# Revit family: Screen-Desk_Mounted-Teknion-JNSASW-Solid_Add-On-R2015
name_source: partatom
category: Furniture
revit_build: Autodesk Revit 2018 (Build: 20190510_1515(x64)
units: mm (PartAtom-declared; Revit-internal decimal feet)

## family parameters
Always vertical = Yes
Cut with Voids When Loaded = No
OmniClass Number = 23.40.20.00
OmniClass Title = General Furniture and Specialties
Room Calculation Point = No
Shared = Yes
Work Plane-Based = No

## types (3) — shared parameters
Assembly Code = E2020200
Manufacturer = Teknion
Manufacturer Fax = 416.661.4586
Part Number = JNSASW
Product Documentation Link = http://www.teknion.com
Product Documentation Link 2 = https://www.teknion.com
Product Documentation Link 3 = https://www.teknion.com
Product Documentation Link 4 = https://www.teknion.com
Product Line = Expansion Cityline
Product Page URL = http://www.teknion.com
Series = Expansion Cityline
Sustainability Data = http://www.teknion.com
URL = www.teknion.com
Unit Weight URL = http://www.teknion.com
Warranty = http://www.teknion.com

## per-type parameters (varying)
| type | Description | Left Offset | Model | Right Offset |
| Standard Width | Solid Add-On Screen – Desk-Mounted, One Side Full Screen or Both Sides Shared Screens Width Reduction for Lateral Application, Standard Corner Detail | 0 " | JNSASW____SS_ | 0 " |
| One Side Full Screen or Both Sides Shared Screens Width Reduction | Solid Add-On Screen – Desk-Mounted, One Side Full Screen or Both Sides Shared Screens Width Reduction for Lateral Application, Standard Corner Detail | 0.945 " | JNSASW____FS_ | 0.945 " |
| One Side Shared Screen Width Reduction | Solid Add-On Screen – Desk-Mounted, One Side Shared Screen Width Reduction for Lateral Application, Standard Corner Detail | 0.473 " | JNSASW____HS_ | 0.473 " |

## geometry (parser evidence)
native form markers: Sweep x2
no freeform markers — native parametric forms only
